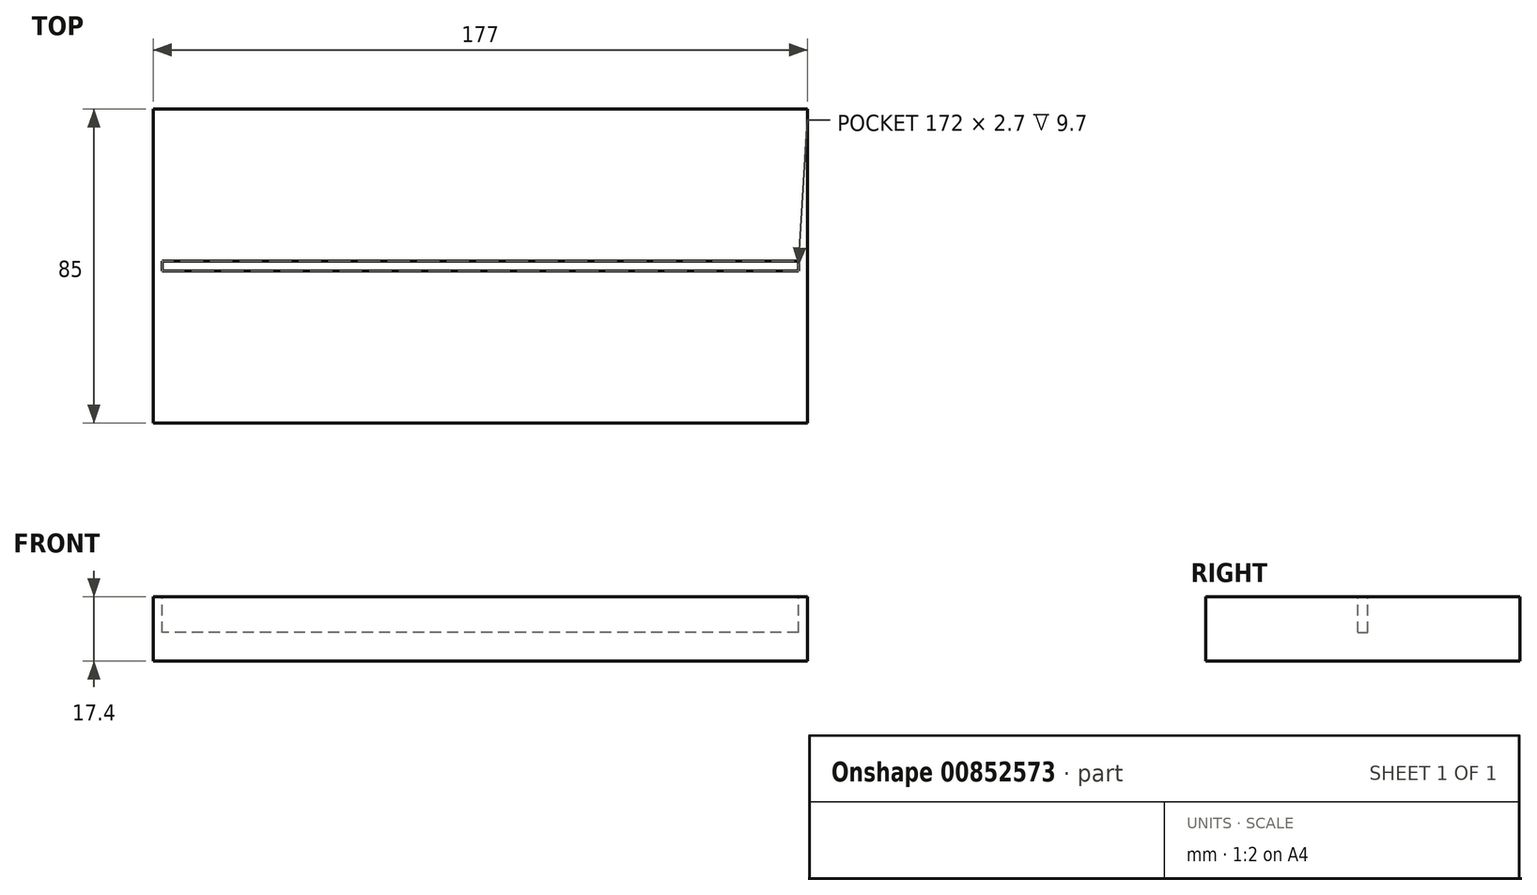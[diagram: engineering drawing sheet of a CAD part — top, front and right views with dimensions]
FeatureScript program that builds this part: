
annotation { "Feature Type Name" : "Feature", "Feature Type Description" : "" }
export const myFeature = defineFeature(function(context is Context, id is Id, definition is map)
    precondition{}
    {
        {
            var Q0;
            Q0=qCreatedBy(makeId("Top.planeOp"),FACE);
            var sketch = newSketch(context, id + "F0", { "sketchPlane" : qUnion([Q0])});
            skLineSegment(sketch, "E0.bottom", {"start": v(88.5, -42.5) * mm, "end": v(-88.5, -42.5) * mm});
            skLineSegment(sketch, "E0.top", {"start": v(88.5, 42.5) * mm, "end": v(-88.5, 42.5) * mm});
            skLineSegment(sketch, "E0.left", {"start": v(88.5, -42.5) * mm, "end": v(88.5, 42.5) * mm});
            skLineSegment(sketch, "E0.right", {"start": v(-88.5, -42.5) * mm, "end": v(-88.5, 42.5) * mm});
            skLineSegment(sketch, "E1", {"start": v(-88.5, 42.5) * mm, "end": v(-88.5, -42.5) * mm});
            skLineSegment(sketch, "E2", {"start": v(88.5, 42.5) * mm, "end": v(88.5, -42.5) * mm});
            skSolve(sketch);
        }
        {
            var Q0;
            {var subQ0=sQuery(id+"F0.wireOp",EDGE,"E0.top");Q0=makeQuery(id+"F0.imprint","IMPRINT",FACE,{"disambiguationData":[TD([[makeQuery(id+"F0.imprint","IMPRINT",EDGE,{"derivedFrom":subQ0}),1.0]])]});}
            var Q1;
            {var subQ0=sQuery(id+"F0.wireOp",EDGE,"E0.bottom");Q1=makeQuery(id+"F0.imprint","IMPRINT",FACE,{"disambiguationData":[TD([[makeQuery(id+"F0.imprint","IMPRINT",EDGE,{"derivedFrom":subQ0}),-1.0]])]});}
            extrude(context, id + "F1", {"entities" : qUnion([Q0, Q1]), "depth" : 17.4 * mm, "offsetDistance" : 25 * mm});
        }
        {
            var Q0;
            Q0=makeQuery(id+"F1.opExtrude","CAP_FACE",FACE,{"disambiguationData":[OSD([sQuery(id+"F0.wireOp",EDGE,"E0.bottom"),sQuery(id+"F0.wireOp",EDGE,"E0.top"),sQuery(id+"F0.wireOp",EDGE,"E1"),sQuery(id+"F0.wireOp",EDGE,"E2")])],"isStart":false});
            var sketch = newSketch(context, id + "F2", { "sketchPlane" : qUnion([Q0])});
            skLineSegment(sketch, "E3.bottom", {"start": v(86, -1.35) * mm, "end": v(-86, -1.35) * mm});
            skLineSegment(sketch, "E3.top", {"start": v(86, 1.35) * mm, "end": v(-86, 1.35) * mm});
            skLineSegment(sketch, "E3.left", {"start": v(86, -1.35) * mm, "end": v(86, 1.35) * mm});
            skLineSegment(sketch, "E3.right", {"start": v(-86, -1.35) * mm, "end": v(-86, 1.35) * mm});
            skPoint(sketch, "E3.middle", {"position": v(0, 0) * mm});
            skSolve(sketch);
        }
        {
            var Q0;
            Q0=makeQuery(id+"F2.imprint","IMPRINT",FACE,{"disambiguationData":[TD([[makeQuery(id+"F2.imprint","IMPRINT",EDGE,{"derivedFrom":sQuery(id+"F2.wireOp",EDGE,"E3.bottom")}),-1.0]])]});
            extrude(context, id + "F3", {"entities" : qUnion([Q0]), "operationType" : NewBodyOperationType.REMOVE, "oppositeDirection" : true, "depth" : 9.7 * mm, "offsetDistance" : 25 * mm});
        }
    });
